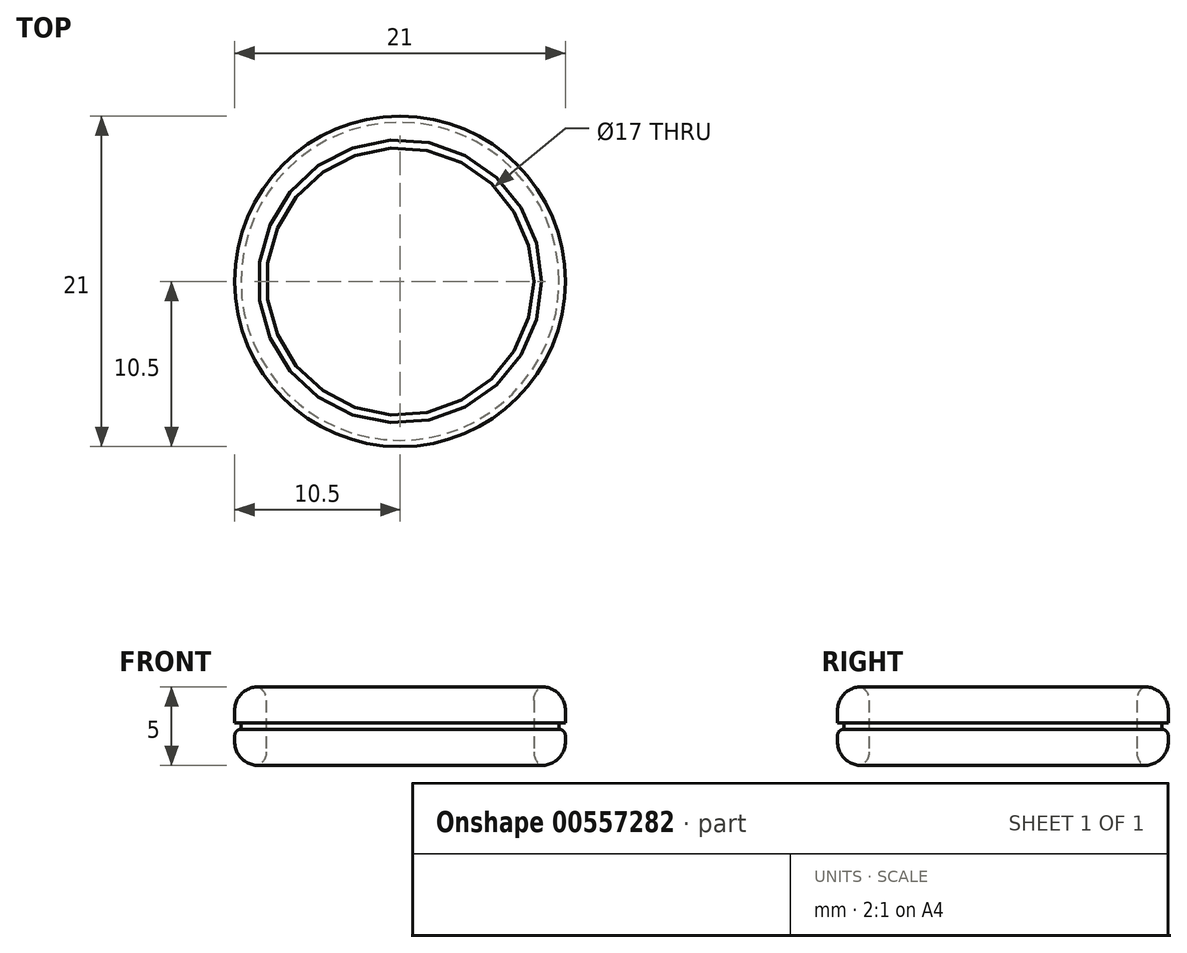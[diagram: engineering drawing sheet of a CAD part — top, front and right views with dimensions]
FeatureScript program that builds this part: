
annotation { "Feature Type Name" : "Feature", "Feature Type Description" : "" }
export const myFeature = defineFeature(function(context is Context, id is Id, definition is map)
    precondition{}
    {
        {
            var Q0;
            Q0=qCreatedBy(makeId("Top.planeOp"),FACE);
            var sketch = newSketch(context, id + "F0", { "sketchPlane" : qUnion([Q0])});
            skCircle(sketch, "E0", {"center": v(0, 0) * mm, "radius": 8.5 * mm});
            skCircle(sketch, "E1", {"center": v(0, 0) * mm, "radius": 10.5 * mm});
            skSolve(sketch);
        }
        {
            var Q0;
            Q0=qSketchRegion(id+"F0",true);
            extrude(context, id + "F1", {"entities" : qUnion([Q0]), "endBound" : BoundingType.SYMMETRIC, "depth" : 5 * mm, "offsetDistance" : 25 * mm});
        }
        {
            var Q0;
            Q0=makeQuery(id+"F1.opExtrude","CAP_EDGE",EDGE,{"disambiguationData":[OSD([sQuery(id+"F0.wireOp",EDGE,"E1")])],"isStart":false});
            var Q1;
            Q1=makeQuery(id+"F1.opExtrude","CAP_EDGE",EDGE,{"disambiguationData":[OSD([sQuery(id+"F0.wireOp",EDGE,"E1")])],"isStart":true});
            fillet(context, id + "F2", {"entities" : qUnion([Q0, Q1]), "radius" : 1.5 * mm, "tangentPropagation" : true, "allowEdgeOverflow" : false});
        }
        {
            var Q0;
            Q0=makeQuery(id+"F1.opExtrude","CAP_EDGE",EDGE,{"disambiguationData":[OSD([sQuery(id+"F0.wireOp",EDGE,"E0")])],"isStart":false});
            var Q1;
            Q1=makeQuery(id+"F1.opExtrude","CAP_EDGE",EDGE,{"disambiguationData":[OSD([sQuery(id+"F0.wireOp",EDGE,"E0")])],"isStart":true});
            fillet(context, id + "F3", {"entities" : qUnion([Q0, Q1]), "radius" : 1 * mm, "tangentPropagation" : true, "rho" : 0.5, "crossSection" : FilletCrossSection.CONIC, "allowEdgeOverflow" : false});
        }
        {
            var Q0;
            Q0=qCreatedBy(makeId("Top.planeOp"),FACE);
            var sketch = newSketch(context, id + "F4", { "sketchPlane" : qUnion([Q0])});
            skCircle(sketch, "E2", {"center": v(0, 0) * mm, "radius": 10.5 * mm});
            skCircle(sketch, "E3", {"center": v(0, 0) * mm, "radius": 10.1 * mm});
            skSolve(sketch);
        }
        {
            var Q0;
            Q0=qSketchRegion(id+"F4",true);
            extrude(context, id + "F5", {"entities" : qUnion([Q0]), "operationType" : NewBodyOperationType.REMOVE, "endBound" : BoundingType.SYMMETRIC, "depth" : 0.4 * mm, "offsetDistance" : 25 * mm});
        }
        {
            var Q0;
            Q0=makeQuery(id+"F5.boolean.opBoolean","COPY",EDGE,{"derivedFrom":makeQuery(id+"F5.opExtrude","CAP_EDGE",EDGE,{"disambiguationData":[OSD([sQuery(id+"F4.wireOp",EDGE,"E2")])],"isStart":false})});
            var Q1;
            Q1=makeQuery(id+"F5.boolean.opBoolean","COPY",EDGE,{"derivedFrom":makeQuery(id+"F5.opExtrude","CAP_EDGE",EDGE,{"disambiguationData":[OSD([sQuery(id+"F4.wireOp",EDGE,"E2")])],"isStart":true})});
            fillet(context, id + "F6", {"entities" : qUnion([Q0, Q1]), "radius" : 0.4 * mm, "tangentPropagation" : true, "allowEdgeOverflow" : false});
        }
    });
